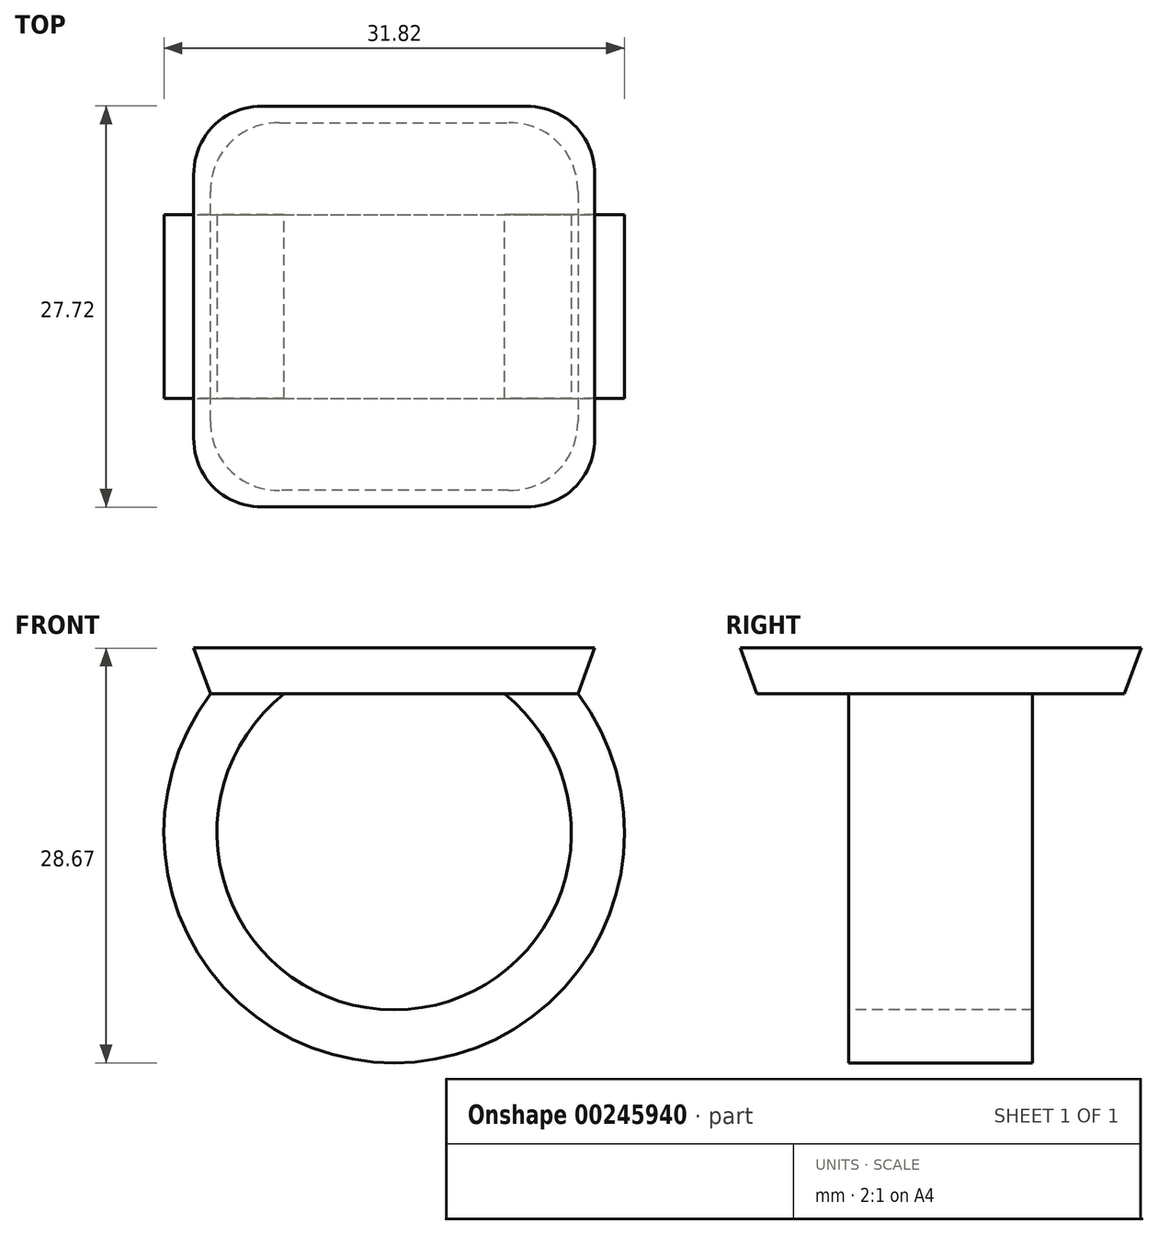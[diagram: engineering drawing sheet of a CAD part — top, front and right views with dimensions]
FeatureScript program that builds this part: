
annotation { "Feature Type Name" : "Feature", "Feature Type Description" : "" }
export const myFeature = defineFeature(function(context is Context, id is Id, definition is map)
    precondition{}
    {
        {
            var Q0;
            Q0=qCreatedBy(makeId("Top.planeOp"),FACE);
            var sketch = newSketch(context, id + "F0", { "sketchPlane" : qUnion([Q0])});
            skLineSegment(sketch, "E0.bottom", {"start": v(-12.7, 12.7) * mm, "end": v(12.7, 12.7) * mm});
            skLineSegment(sketch, "E0.top", {"start": v(-12.7, -12.7) * mm, "end": v(12.7, -12.7) * mm});
            skLineSegment(sketch, "E0.left", {"start": v(-12.7, 12.7) * mm, "end": v(-12.7, -12.7) * mm});
            skLineSegment(sketch, "E0.right", {"start": v(12.7, 12.7) * mm, "end": v(12.7, -12.7) * mm});
            skPoint(sketch, "E0.middle", {"position": v(0, 0) * mm});
            skSolve(sketch);
        }
        {
            var Q0;
            Q0 = qSketchRegion(id + "F0", true);
            extrude(context, id + "F1", {"entities" : qUnion([Q0]), "depth" : 3.17 * mm, "hasDraft" : true, "draftAngle" : 20 * degree});
        }
        {
            var Q0;
            Q0=qCreatedBy(makeId("Front.planeOp"),FACE);
            var sketch = newSketch(context, id + "F2", { "sketchPlane" : qUnion([Q0])});
            skArc(sketch, "E1", {"start": v(-10.16, 0) * mm, "mid": v(0, -23.56) * mm, "end": v(10.16, 0) * mm});
            skSolve(sketch);
        }
        {
            var Q0;
            Q0=makeQuery(id+"F1.opExtrude","CAP_FACE",FACE,{"disambiguationData":[OSD([sQuery(id+"F0.wireOp",EDGE,"E0.bottom"),sQuery(id+"F0.wireOp",EDGE,"E0.top"),sQuery(id+"F0.wireOp",EDGE,"E0.left"),sQuery(id+"F0.wireOp",EDGE,"E0.right")])],"isStart":true});
            var sketch = newSketch(context, id + "F3", { "sketchPlane" : qUnion([Q0])});
            skLineSegment(sketch, "E2.bottom", {"start": v(-12.7, 6.35) * mm, "end": v(-7.62, 6.35) * mm});
            skLineSegment(sketch, "E2.top", {"start": v(-12.7, -6.35) * mm, "end": v(-7.62, -6.35) * mm});
            skLineSegment(sketch, "E2.left", {"start": v(-12.7, 6.35) * mm, "end": v(-12.7, -6.35) * mm});
            skLineSegment(sketch, "E2.right", {"start": v(-7.62, 6.35) * mm, "end": v(-7.62, -6.35) * mm});
            skPoint(sketch, "E2.middle", {"position": v(-10.16, 0) * mm});
            skPoint(sketch, "E2.middle.positionSnap0", {"position": v(12.7, 0) * mm});
            skPoint(sketch, "E2.centerSnap0", {"position": v(12.7, 0) * mm});
            skSolve(sketch);
        }
        {
            var Q0;
            Q0=makeQuery(id+"F3.imprint","IMPRINT",FACE,{"disambiguationData":[TD([[makeQuery(id+"F3.imprint","IMPRINT",EDGE,{"derivedFrom":sQuery(id+"F3.wireOp",EDGE,"E2.bottom")}),-1.0]])]});
            var Q1;
            Q1=sQuery(id+"F2.wireOp",EDGE,"E1");
            sweep(context, id + "F4", {"operationType" : NewBodyOperationType.ADD, "profiles" : qUnion([Q0]), "path" : qUnion([Q1])});
        }
        {
            var Q0;
            Q0=qCreatedBy(makeId("Front.planeOp"),FACE);
            var sketch = newSketch(context, id + "F5", { "sketchPlane" : qUnion([Q0])});
            skLineSegment(sketch, "E3.0", {"start": v(7.62, 0) * mm, "end": v(10.16, 0) * mm});
            skLineSegment(sketch, "E4.0", {"start": v(10.01, -2.54) * mm, "end": v(10.16, 0) * mm});
            skArc(sketch, "E5", {"start": v(10.01, -2.54) * mm, "mid": v(8.9, -1.18) * mm, "end": v(7.62, 0) * mm});
            skSolve(sketch);
        }
        {
            var Q0;
            Q0=makeQuery(id+"F5.imprint","IMPRINT",FACE,{"disambiguationData":[TD([[makeQuery(id+"F5.imprint","IMPRINT",EDGE,{"derivedFrom":sQuery(id+"F5.wireOp",EDGE,"E3.0")}),-1.0]])]});
            extrude(context, id + "F6", {"entities" : qUnion([Q0]), "operationType" : NewBodyOperationType.ADD, "endBound" : BoundingType.SYMMETRIC, "depth" : 12.7 * mm});
        }
        {
            var Q0;
            Q0=makeQuery(id+"F1.opExtrude","SWEPT_EDGE",EDGE,{"disambiguationData":[OSD([sQuery(id+"F0.wireOp",EDGE,"E0.top"),sQuery(id+"F0.wireOp",EDGE,"E0.left")])]});
            var Q1;
            Q1=makeQuery(id+"F1.opExtrude","SWEPT_EDGE",EDGE,{"disambiguationData":[OSD([sQuery(id+"F0.wireOp",EDGE,"E0.top"),sQuery(id+"F0.wireOp",EDGE,"E0.right")])]});
            var Q2;
            Q2=makeQuery(id+"F1.opExtrude","SWEPT_EDGE",EDGE,{"disambiguationData":[OSD([sQuery(id+"F0.wireOp",EDGE,"E0.bottom"),sQuery(id+"F0.wireOp",EDGE,"E0.right")])]});
            var Q3;
            Q3=makeQuery(id+"F1.opExtrude","SWEPT_EDGE",EDGE,{"disambiguationData":[OSD([sQuery(id+"F0.wireOp",EDGE,"E0.bottom"),sQuery(id+"F0.wireOp",EDGE,"E0.left")])]});
            fillet(context, id + "F7", {"entities" : qUnion([Q0, Q1, Q2, Q3]), "radius" : 5.08 * mm, "tangentPropagation" : true, "allowEdgeOverflow" : false});
        }
    });
